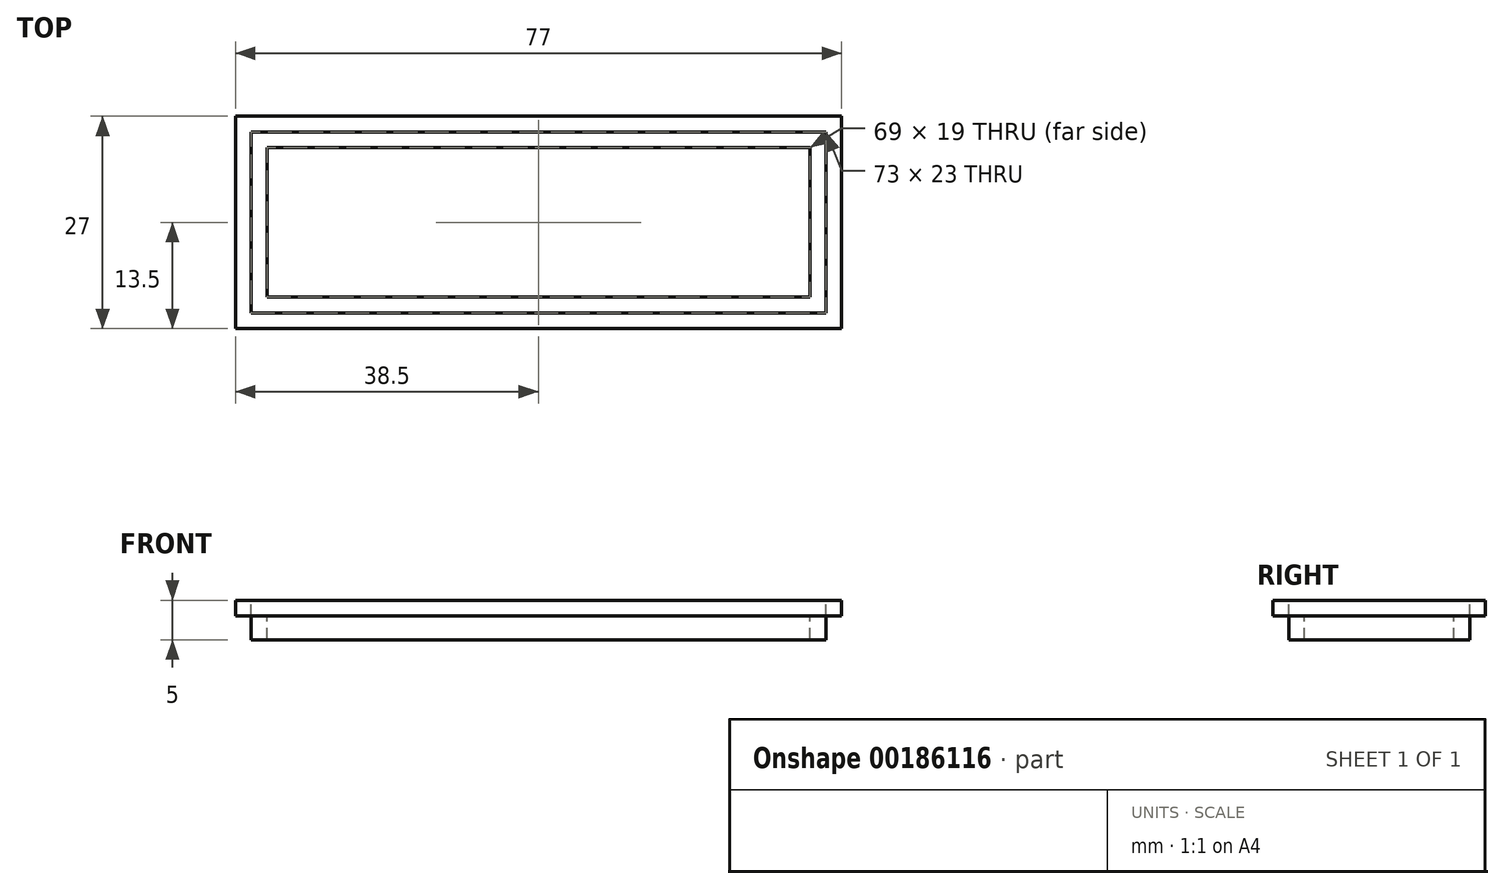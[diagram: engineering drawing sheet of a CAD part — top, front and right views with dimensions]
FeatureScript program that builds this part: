
annotation { "Feature Type Name" : "Feature", "Feature Type Description" : "" }
export const myFeature = defineFeature(function(context is Context, id is Id, definition is map)
    precondition{}
    {
        {
            var Q0;
            Q0=qCreatedBy(makeId("Top.planeOp"),FACE);
            var sketch = newSketch(context, id + "F0", { "sketchPlane" : qUnion([Q0])});
            skLineSegment(sketch, "E0.bottom", {"start": v(0, 0) * mm, "end": v(73, 0) * mm});
            skLineSegment(sketch, "E0.top", {"start": v(0, 23) * mm, "end": v(73, 23) * mm});
            skLineSegment(sketch, "E0.left", {"start": v(0, 0) * mm, "end": v(0, 23) * mm});
            skLineSegment(sketch, "E0.right", {"start": v(73, 0) * mm, "end": v(73, 23) * mm});
            skSolve(sketch);
        }
        {
            var Q0;
            Q0 = qSketchRegion(id + "F0", true);
            extrude(context, id + "F1", {"entities" : qUnion([Q0]), "depth" : 3 * mm});
        }
        {
            var Q0;
            Q0=makeQuery(id+"F1.opExtrude","CAP_FACE",FACE,{"disambiguationData":[OSD([sQuery(id+"F0.wireOp",EDGE,"E0.bottom"),sQuery(id+"F0.wireOp",EDGE,"E0.top"),sQuery(id+"F0.wireOp",EDGE,"E0.left"),sQuery(id+"F0.wireOp",EDGE,"E0.right")])],"isStart":false});
            var sketch = newSketch(context, id + "F2", { "sketchPlane" : qUnion([Q0])});
            skLineSegment(sketch, "E1.0", {"start": v(2, 2) * mm, "end": v(71, 2) * mm});
            skLineSegment(sketch, "E1.1", {"start": v(2, 2) * mm, "end": v(2, 21) * mm});
            skLineSegment(sketch, "E1.2", {"start": v(2, 21) * mm, "end": v(71, 21) * mm});
            skLineSegment(sketch, "E1.3", {"start": v(71, 2) * mm, "end": v(71, 21) * mm});
            skSolve(sketch);
        }
        {
            var Q0;
            Q0 = qSketchRegion(id + "F2", true);
            extrude(context, id + "F3", {"entities" : qUnion([Q0]), "operationType" : NewBodyOperationType.REMOVE, "oppositeDirection" : true, "depth" : 3 * mm});
        }
        {
            var Q0;
            Q0=makeQuery(id+"F1.opExtrude","CAP_FACE",FACE,{"disambiguationData":[OSD([sQuery(id+"F0.wireOp",EDGE,"E0.bottom"),sQuery(id+"F0.wireOp",EDGE,"E0.top"),sQuery(id+"F0.wireOp",EDGE,"E0.left"),sQuery(id+"F0.wireOp",EDGE,"E0.right")])],"isStart":false});
            var sketch = newSketch(context, id + "F4", { "sketchPlane" : qUnion([Q0])});
            skLineSegment(sketch, "E2.0", {"start": v(-2, -2) * mm, "end": v(-2, 25) * mm});
            skLineSegment(sketch, "E2.1", {"start": v(-2, -2) * mm, "end": v(75, -2) * mm});
            skLineSegment(sketch, "E2.2", {"start": v(75, -2) * mm, "end": v(75, 25) * mm});
            skLineSegment(sketch, "E2.3", {"start": v(-2, 25) * mm, "end": v(75, 25) * mm});
            skSolve(sketch);
        }
        {
            var Q0;
            Q0 = qSketchRegion(id + "F4", true);
            extrude(context, id + "F5", {"entities" : qUnion([Q0]), "operationType" : NewBodyOperationType.ADD, "depth" : 2 * mm});
        }
        {
            var Q0;
            Q0=makeQuery(id+"F5.opExtrude","CAP_FACE",FACE,{"disambiguationData":[OSD([sQuery(id+"F4.wireOp",EDGE,"E2.0"),sQuery(id+"F4.wireOp",EDGE,"E2.1"),sQuery(id+"F4.wireOp",EDGE,"E2.2"),sQuery(id+"F4.wireOp",EDGE,"E2.3")])],"isStart":false});
            var sketch = newSketch(context, id + "F6", { "sketchPlane" : qUnion([Q0])});
            skLineSegment(sketch, "E3.0", {"start": v(0, 0) * mm, "end": v(0, 23) * mm});
            skLineSegment(sketch, "E3.1", {"start": v(0, 0) * mm, "end": v(73, 0) * mm});
            skLineSegment(sketch, "E3.2", {"start": v(73, 0) * mm, "end": v(73, 23) * mm});
            skLineSegment(sketch, "E3.3", {"start": v(0, 23) * mm, "end": v(73, 23) * mm});
            skSolve(sketch);
        }
        {
            var Q0;
            Q0 = qSketchRegion(id + "F6", true);
            extrude(context, id + "F7", {"entities" : qUnion([Q0]), "operationType" : NewBodyOperationType.REMOVE, "oppositeDirection" : true, "depth" : 2 * mm});
        }
    });
